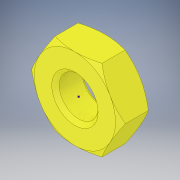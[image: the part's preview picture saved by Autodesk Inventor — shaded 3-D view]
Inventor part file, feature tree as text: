
AUTODESK INVENTOR PART (.ipt)
format: ipt  version: 2018 (Build 220112000, 112)  size: 159,232 bytes
history: native  units: in
note: dims shown in document units (in); Inventor stores cm internally (conversion verified against a paired STEP export)
features: other x3, imported_body x2, plane x1, sketch x1
ambient origin geometry x8: Origin, YZ Plane, XZ Plane, XY Plane, X Axis, Y Axis, Z Axis, Center Point
bodies: Solid1 (feature_tree), Solid2 (feature_tree)
feature tree (7):
  other  "Repaired Geometry1"
  other  "Work Axis1"
  other  "Work Axis2"
  plane  "Work Plane1"
  sketch  "3D Sketch1"
  imported_body  "Base1"
  imported_body  "Base2"
